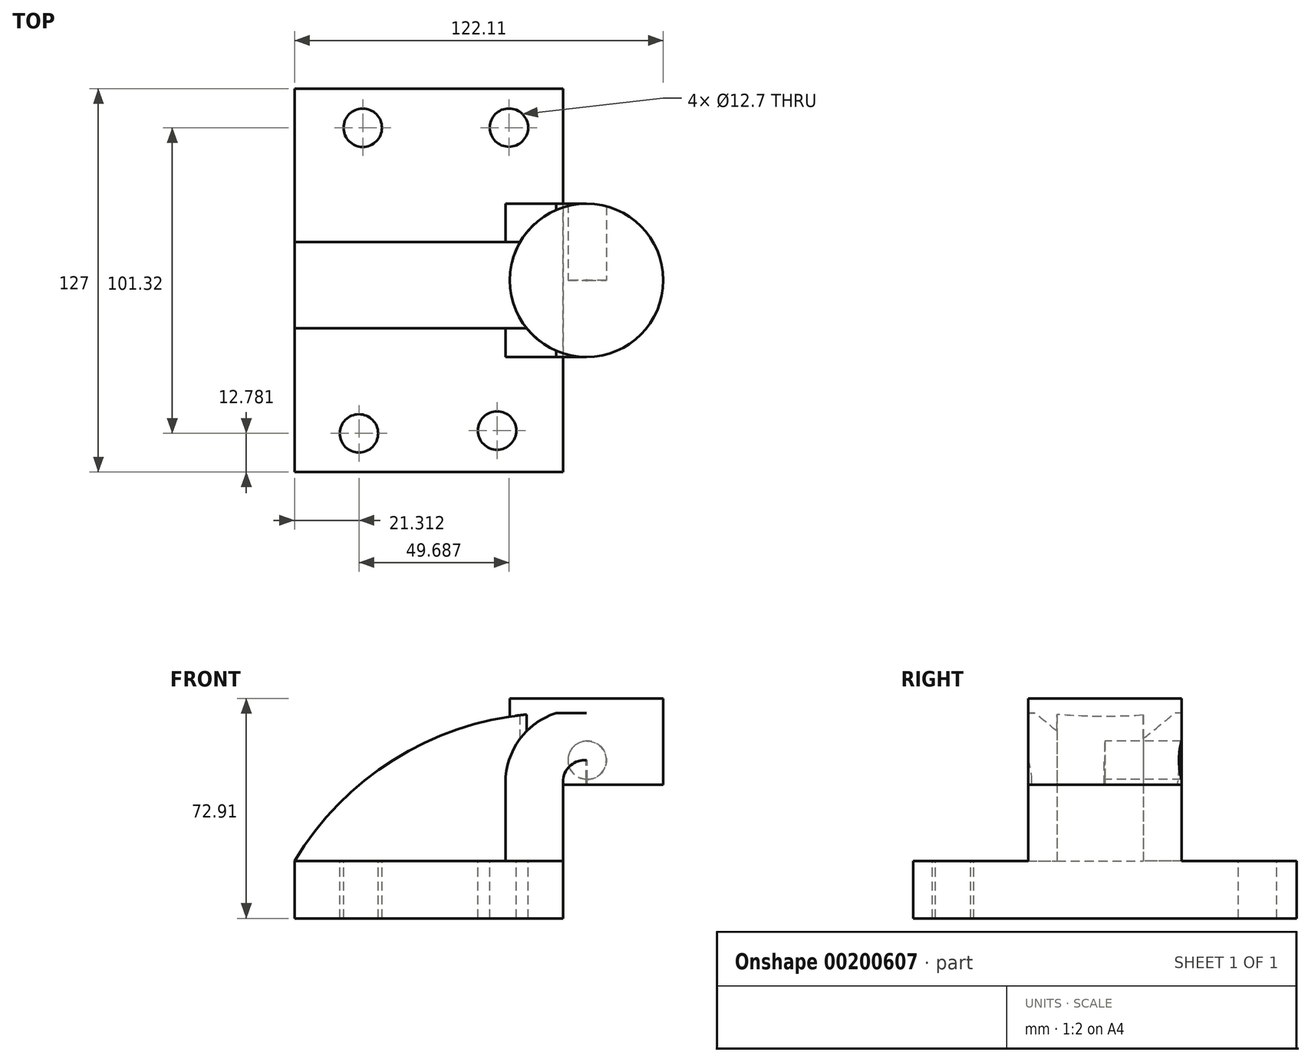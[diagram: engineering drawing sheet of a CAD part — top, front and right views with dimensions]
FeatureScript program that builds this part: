
annotation { "Feature Type Name" : "Feature", "Feature Type Description" : "" }
export const myFeature = defineFeature(function(context is Context, id is Id, definition is map)
    precondition{}
    {
        {
            var Q0;
            Q0=qCreatedBy(makeId("Front.planeOp"),FACE);
            var sketch = newSketch(context, id + "F0", { "sketchPlane" : qUnion([Q0])});
            skLineSegment(sketch, "E0.bottom", {"start": v(-36.03, -19.05) * mm, "end": v(52.87, -19.05) * mm});
            skLineSegment(sketch, "E0.top", {"start": v(-36.03, 0) * mm, "end": v(52.87, 0) * mm});
            skLineSegment(sketch, "E0.left", {"start": v(-36.03, -19.05) * mm, "end": v(-36.03, 0) * mm});
            skLineSegment(sketch, "E0.right", {"start": v(52.87, -19.05) * mm, "end": v(52.87, 0) * mm});
            skArc(sketch, "E1.trimOffspring", {"start": v(56.76, 39.4) * mm, "mid": v(56.7, 39.26) * mm, "end": v(56.64, 39.12) * mm});
            skPoint(sketch, "E2.orphan", {"position": v(56.73, 45.38) * mm});
            skPoint(sketch, "E3.right.end.orphan", {"position": v(39.3, 45.38) * mm});
            skPoint(sketch, "E4.start.orphan", {"position": v(48.02, 45.38) * mm});
            skLineSegment(sketch, "E5.left", {"start": v(75, 36.07) * mm, "end": v(75, 40.08) * mm});
            skLineSegment(sketch, "E6", {"start": v(52.87, 0) * mm, "end": v(52.87, 26.2) * mm});
            skLineSegment(sketch, "E7", {"start": v(74.81, 36.07) * mm, "end": v(75, 36.07) * mm});
            skPoint(sketch, "E8.startSnap0", {"position": v(50.94, 28.04) * mm});
            skPoint(sketch, "E8.start.orphan", {"position": v(21.18, 28.04) * mm});
            skPoint(sketch, "E9.orphan", {"position": v(50.94, 34.31) * mm});
            skPoint(sketch, "E5.top.end.orphan", {"position": v(50.94, 21.78) * mm});
            skLineSegment(sketch, "E10.bottom", {"start": v(86.08, 53.86) * mm, "end": v(60.68, 53.86) * mm});
            skLineSegment(sketch, "E10.top", {"start": v(86.08, 25.29) * mm, "end": v(60.68, 25.29) * mm});
            skLineSegment(sketch, "E10.right", {"start": v(60.68, 53.86) * mm, "end": v(60.68, 25.29) * mm});
            skPoint(sketch, "E10.middle", {"position": v(86.08, 39.57) * mm});
            skLineSegment(sketch, "E11", {"start": v(60.87, 25.29) * mm, "end": v(60.87, 33.35) * mm});
            skLineSegment(sketch, "E12", {"start": v(60.87, 33.35) * mm, "end": v(60.03, 33.35) * mm});
            skArc(sketch, "E13", {"start": v(60.03, 33.35) * mm, "mid": v(54.96, 31.25) * mm, "end": v(52.87, 26.2) * mm});
            skPoint(sketch, "E14.orphan", {"position": v(97.38, -19.05) * mm});
            skPoint(sketch, "E15.start.orphan", {"position": v(65.18, 0) * mm});
            skPoint(sketch, "E16.end.orphan", {"position": v(97.32, -19.05) * mm});
            skLineSegment(sketch, "E17", {"start": v(60.44, 48.98) * mm, "end": v(60.68, 48.98) * mm});
            skLineSegment(sketch, "E18", {"start": v(52.87, 17.5) * mm, "end": v(33.82, 17.5) * mm});
            skLineSegment(sketch, "E19", {"start": v(33.82, 25.94) * mm, "end": v(33.82, 0) * mm});
            skLineSegment(sketch, "E20", {"start": v(60.68, 48.98) * mm, "end": v(50.6, 48.98) * mm});
            skArc(sketch, "E21", {"start": v(50.6, 48.98) * mm, "mid": v(38.46, 40.19) * mm, "end": v(33.82, 25.94) * mm});
            skArc(sketch, "E22", {"start": v(50.6, 48.98) * mm, "mid": v(0.83, 35.89) * mm, "end": v(-36.03, 0) * mm});
            skPoint(sketch, "E23.end.orphan", {"position": v(56.73, 67.73) * mm});
            skLineSegment(sketch, "E24", {"start": v(86.08, 25.29) * mm, "end": v(86.08, 53.86) * mm});
            skLineSegment(sketch, "E25", {"start": v(60.68, 48.98) * mm, "end": v(67.22, 48.98) * mm});
            skLineSegment(sketch, "E26", {"start": v(60.87, 33.35) * mm, "end": v(66.12, 33.35) * mm});
            skPoint(sketch, "E27.end.orphan", {"position": v(111.48, 53.86) * mm});
            skPoint(sketch, "E28.orphan", {"position": v(111.48, 25.29) * mm});
            skSolve(sketch);
        }
        {
            var Q0;
            Q0=makeQuery(id+"F0.imprint","IMPRINT",FACE,{"disambiguationData":[TD([[makeQuery(id+"F0.imprint","IMPRINT",EDGE,{"derivedFrom":sQuery(id+"F0.wireOp",EDGE,"E0.bottom")}),1.0]])]});
            extrude(context, id + "F1", {"entities" : qUnion([Q0]), "depth" : 63.5 * mm});
        }
        {
            var Q0;
            {var subQ5=sQuery(id+"F0.wireOp",EDGE,"E21");Q0=makeQuery(id+"F0.imprint","IMPRINT",FACE,{"disambiguationData":[TD([[makeQuery(id+"F0.imprint","IMPRINT",EDGE,{"derivedFrom":subQ5}),-1.0]])]});}
            extrude(context, id + "F2", {"entities" : qUnion([Q0]), "operationType" : NewBodyOperationType.ADD, "depth" : 15.88 * mm});
        }
        {
            var Q0;
            Q0=makeQuery(id+"F0.imprint","IMPRINT",FACE,{"disambiguationData":[TD([[makeQuery(id+"F0.imprint","IMPRINT",EDGE,{"derivedFrom":sQuery(id+"F0.wireOp",EDGE,"E0.bottom")}),1.0]])]});
            extrude(context, id + "F3", {"entities" : qUnion([Q0]), "operationType" : NewBodyOperationType.ADD, "oppositeDirection" : true, "depth" : 63.5 * mm});
        }
        {
            var Q0;
            {var subQ5=sQuery(id+"F0.wireOp",EDGE,"E13");Q0=makeQuery(id+"F0.imprint","IMPRINT",FACE,{"disambiguationData":[TD([[makeQuery(id+"F0.imprint","IMPRINT",EDGE,{"derivedFrom":subQ5}),-1.0]])]});}
            var Q1;
            {var subQ5=sQuery(id+"F0.wireOp",EDGE,"E18");Q1=makeQuery(id+"F0.imprint","IMPRINT",FACE,{"disambiguationData":[TD([[makeQuery(id+"F0.imprint","IMPRINT",EDGE,{"derivedFrom":subQ5}),1.0]])]});}
            extrude(context, id + "F4", {"entities" : qUnion([Q0, Q1]), "operationType" : NewBodyOperationType.ADD, "depth" : 25.4 * mm});
        }
        {
            var Q0;
            {var subQ5=sQuery(id+"F0.wireOp",EDGE,"E13");Q0=makeQuery(id+"F0.imprint","IMPRINT",FACE,{"disambiguationData":[TD([[makeQuery(id+"F0.imprint","IMPRINT",EDGE,{"derivedFrom":subQ5}),-1.0]])]});}
            var Q1;
            {var subQ5=sQuery(id+"F0.wireOp",EDGE,"E18");Q1=makeQuery(id+"F0.imprint","IMPRINT",FACE,{"disambiguationData":[TD([[makeQuery(id+"F0.imprint","IMPRINT",EDGE,{"derivedFrom":subQ5}),1.0]])]});}
            extrude(context, id + "F5", {"entities" : qUnion([Q0, Q1]), "operationType" : NewBodyOperationType.ADD, "oppositeDirection" : true, "depth" : 25.4 * mm});
        }
        {
            var Q0;
            {var subQ5=sQuery(id+"F0.wireOp",EDGE,"E18");Q0=makeQuery(id+"F0.imprint","IMPRINT",FACE,{"disambiguationData":[TD([[makeQuery(id+"F0.imprint","IMPRINT",EDGE,{"derivedFrom":subQ5}),1.0]])]});}
            extrude(context, id + "F6", {"entities" : qUnion([Q0]), "operationType" : NewBodyOperationType.ADD, "oppositeDirection" : true, "depth" : 25.4 * mm});
        }
        {
            var Q0;
            {var subQ0=sQuery(id+"F0.wireOp",EDGE,"E21");Q0=makeQuery(id+"F0.imprint","IMPRINT",FACE,{"disambiguationData":[TD([[makeQuery(id+"F0.imprint","IMPRINT",EDGE,{"derivedFrom":subQ0}),-1.0]])]});}
            extrude(context, id + "F7", {"entities" : qUnion([Q0]), "operationType" : NewBodyOperationType.ADD, "oppositeDirection" : true, "depth" : 12.7 * mm});
        }
        {
            var Q0;
            {var subQ6=sQuery(id+"F0.wireOp",EDGE,"E11");Q0=makeQuery(id+"F0.imprint","IMPRINT",FACE,{"disambiguationData":[TD([[makeQuery(id+"F0.imprint","IMPRINT",EDGE,{"derivedFrom":subQ6}),-1.0]])]});}
            var Q1;
            Q1=sQuery(id+"F0.wireOp",EDGE,"E10.right");
            revolve(context, id + "F8", {"operationType" : NewBodyOperationType.ADD, "entities" : qUnion([Q0]), "axis" : qUnion([Q1]), "revolveType" : RevolveType.FULL});
        }
        {
            var Q0;
            {var subQ3=sQuery(id+"F0.wireOp",EDGE,"E0.top");var subQ4=sQuery(id+"F0.wireOp",EDGE,"E0.right");var subQ5=sQuery(id+"F0.wireOp",EDGE,"E0.left");var subQ6=sQuery(id+"F0.wireOp",EDGE,"E0.bottom");Q0=makeQuery(id+"F4.boolean.opBoolean","SPLIT",FACE,{"disambiguationData":[TD([makeQuery(id+"F1.opExtrude","CAP_FACE",FACE,{"disambiguationData":[OSD([subQ6,subQ3,subQ5,subQ4])],"isStart":true})])],"derivedFrom":makeQuery(id+"F3.boolean.opBoolean","MERGE",FACE,{"derivedFrom":[makeQuery(id+"F1.opExtrude","SWEPT_FACE",FACE,{"disambiguationData":[OSD([subQ3])]}),makeQuery(id+"F3.opExtrude","SWEPT_FACE",FACE,{"disambiguationData":[OSD([subQ3])]})]})});}
            var sketch = newSketch(context, id + "F9", { "sketchPlane" : qUnion([Q0])});
            skCircle(sketch, "E29", {"center": v(-13.45, 50.56) * mm, "radius": 12.7 * mm});
            skCircle(sketch, "E30", {"center": v(34.97, 50.6) * mm, "radius": 12.7 * mm});
            skCircle(sketch, "E31", {"center": v(-14.72, -50.72) * mm, "radius": 12.7 * mm});
            skCircle(sketch, "E32", {"center": v(31.03, -49.77) * mm, "radius": 12.7 * mm});
            skCircle(sketch, "E33", {"center": v(60.47, 0) * mm, "radius": 2.84 * mm});
            skSolve(sketch);
        }
        {
            var Q0;
            Q0=sQuery(id+"F9.wireOp",VERTEX,"E29.center");
            var Q1;
            Q1=sQuery(id+"F9.wireOp",VERTEX,"E30.center");
            var Q2;
            Q2=sQuery(id+"F9.wireOp",VERTEX,"E32.center");
            var Q3;
            Q3=sQuery(id+"F9.wireOp",VERTEX,"E31.center");
            var Q4;
            Q4=sQuery(id+"F0.wireOp",VERTEX,"E12.start");
            var Q5;
            Q5=makeQuery(id+"F1.opExtrude","SWEPT_BODY",BODY,{"disambiguationData":[OSD([sQuery(id+"F0.wireOp",EDGE,"E0.bottom"),sQuery(id+"F0.wireOp",EDGE,"E0.top"),sQuery(id+"F0.wireOp",EDGE,"E0.left"),sQuery(id+"F0.wireOp",EDGE,"E0.right")])]});
            hole(context, id + "F10", {"style" : HoleStyle.SIMPLE, "endStyle" : HoleEndStyle.THROUGH, "holeDiameter" : 12.7 * mm, "locations" : qUnion([Q0, Q1, Q2, Q3, Q4]), "scope" : qUnion([Q5]), "isTappedThrough" : true});
        }
    });
